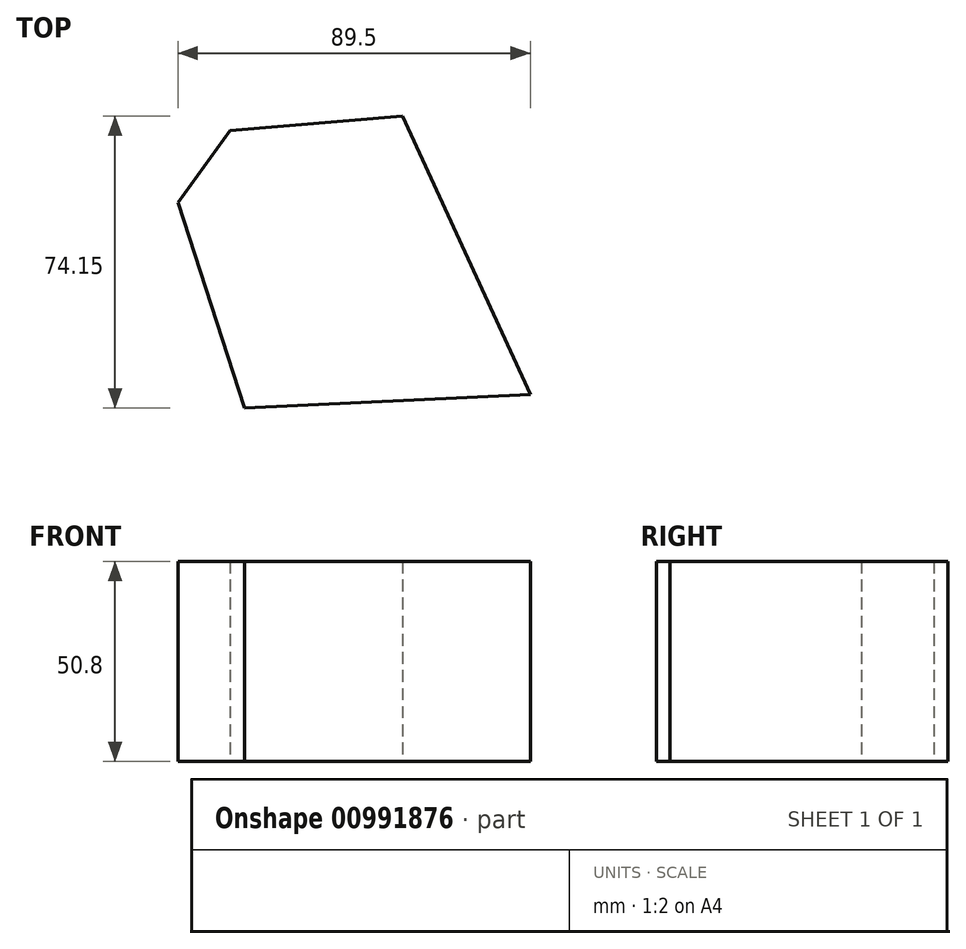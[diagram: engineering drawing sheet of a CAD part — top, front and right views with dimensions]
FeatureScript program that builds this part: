
annotation { "Feature Type Name" : "Feature", "Feature Type Description" : "" }
export const myFeature = defineFeature(function(context is Context, id is Id, definition is map)
    precondition{}
    {
        {
            var Q0;
            Q0=qCreatedBy(makeId("Top.planeOp"),FACE);
            var sketch = newSketch(context, id + "F0", { "sketchPlane" : qUnion([Q0])});
            skLineSegment(sketch, "E0", {"start": v(-43.23, 20.85) * mm, "end": v(-30.05, 39.24) * mm});
            skLineSegment(sketch, "E1", {"start": v(-30.05, 39.24) * mm, "end": v(13.83, 42.87) * mm});
            skLineSegment(sketch, "E2", {"start": v(13.83, 42.87) * mm, "end": v(46.27, -27.8) * mm});
            skLineSegment(sketch, "E3", {"start": v(46.27, -27.8) * mm, "end": v(-26.28, -31.28) * mm});
            skLineSegment(sketch, "E4", {"start": v(-26.28, -31.28) * mm, "end": v(-43.23, 20.85) * mm});
            skSolve(sketch);
        }
        {
            var Q0;
            Q0 = qSketchRegion(id + "F0", true);
            extrude(context, id + "F1", {"entities" : qUnion([Q0]), "depth" : 50.8 * mm, "offsetDistance" : 25.4 * mm});
        }
    });
